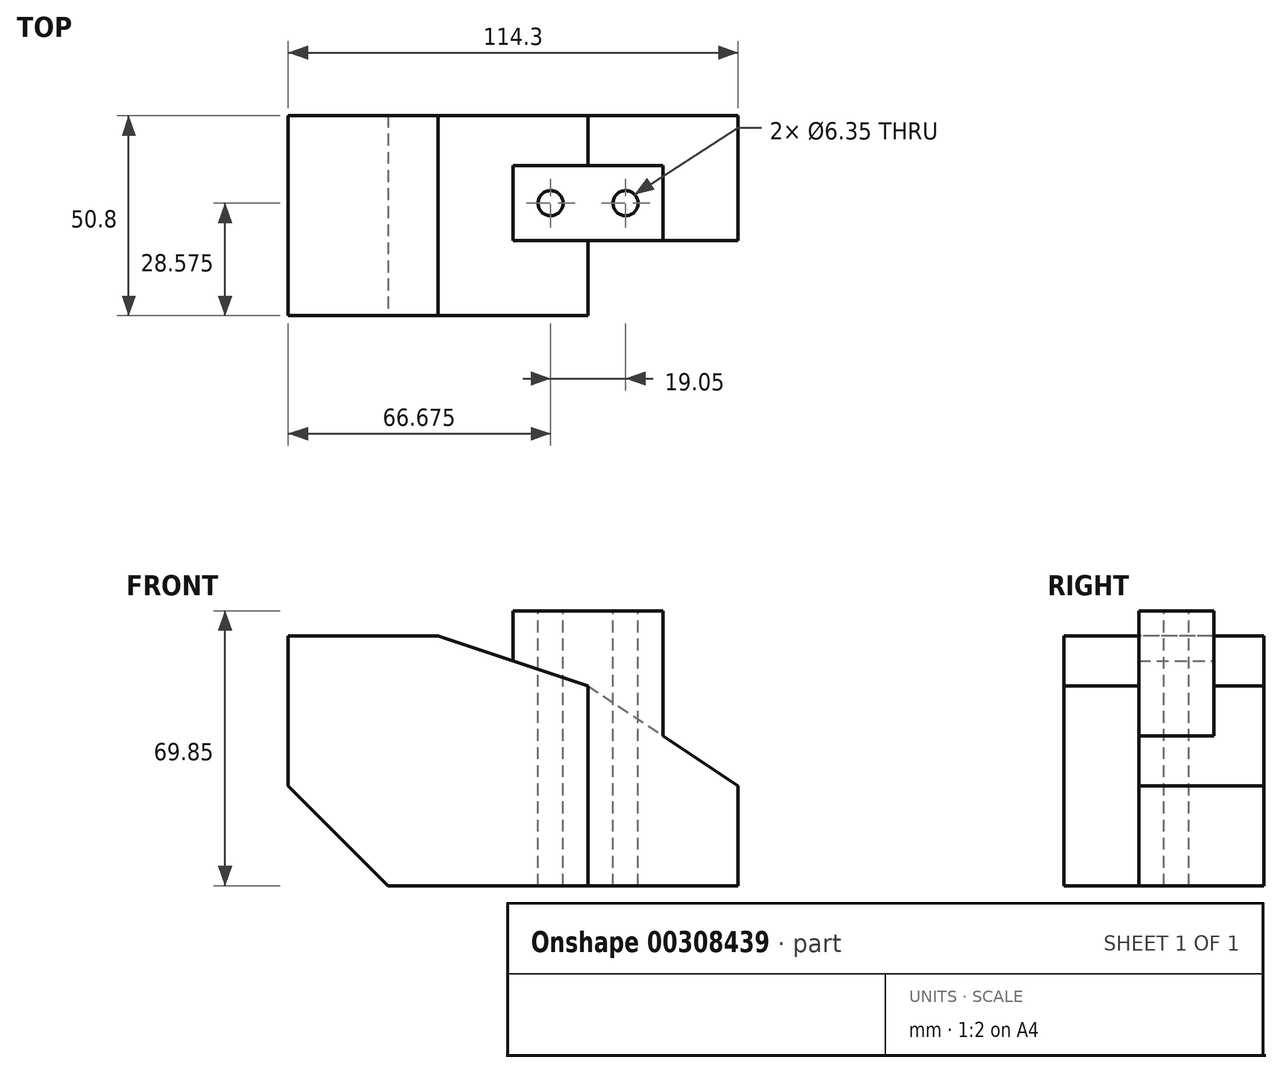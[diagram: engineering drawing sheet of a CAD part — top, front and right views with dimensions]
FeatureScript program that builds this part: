
annotation { "Feature Type Name" : "Feature", "Feature Type Description" : "" }
export const myFeature = defineFeature(function(context is Context, id is Id, definition is map)
    precondition{}
    {
        {
            var Q0;
            Q0=qCreatedBy(makeId("Front.planeOp"),FACE);
            var sketch = newSketch(context, id + "F0", { "sketchPlane" : qUnion([Q0])});
            skLineSegment(sketch, "E0", {"start": v(0, 0) * mm, "end": v(0, 38.1) * mm});
            skLineSegment(sketch, "E1", {"start": v(0, 0) * mm, "end": v(25.4, -25.4) * mm});
            skLineSegment(sketch, "E2", {"start": v(25.4, -25.4) * mm, "end": v(76.2, -25.4) * mm});
            skLineSegment(sketch, "E3", {"start": v(76.2, -25.4) * mm, "end": v(114.3, -25.4) * mm});
            skLineSegment(sketch, "E4", {"start": v(114.3, -25.4) * mm, "end": v(114.3, 38.1) * mm});
            skLineSegment(sketch, "E5", {"start": v(0, 38.1) * mm, "end": v(114.3, 38.1) * mm});
            skSolve(sketch);
        }
        {
            var Q0;
            Q0 = qSketchRegion(id + "F0", true);
            extrude(context, id + "F1", {"entities" : qUnion([Q0]), "oppositeDirection" : true, "depth" : 50.8 * mm});
        }
        {
            var Q0;
            Q0=qCreatedBy(makeId("Top.planeOp"),FACE);
            var sketch = newSketch(context, id + "F2", { "sketchPlane" : qUnion([Q0])});
            skLineSegment(sketch, "E6", {"start": v(114.3, 0) * mm, "end": v(114.3, 19.05) * mm});
            skLineSegment(sketch, "E7", {"start": v(114.3, 0) * mm, "end": v(76.2, 0) * mm});
            skLineSegment(sketch, "E8", {"start": v(76.2, 0) * mm, "end": v(76.2, 19.05) * mm});
            skLineSegment(sketch, "E9", {"start": v(76.2, 19.05) * mm, "end": v(114.3, 19.05) * mm});
            skSolve(sketch);
        }
        {
            var Q0;
            Q0 = qSketchRegion(id + "F2", true);
            extrude(context, id + "F3", {"entities" : qUnion([Q0]), "operationType" : NewBodyOperationType.REMOVE, "endBound" : BoundingType.SYMMETRIC, "oppositeDirection" : true, "depth" : 254 * mm});
        }
        {
            var Q0;
            Q0=qCreatedBy(makeId("Front.planeOp"),FACE);
            var sketch = newSketch(context, id + "F4", { "sketchPlane" : qUnion([Q0])});
            skLineSegment(sketch, "E10", {"start": v(76.2, 38.1) * mm, "end": v(38.1, 38.1) * mm});
            skLineSegment(sketch, "E11", {"start": v(76.2, 38.1) * mm, "end": v(76.2, 25.4) * mm});
            skLineSegment(sketch, "E12", {"start": v(38.1, 38.1) * mm, "end": v(76.2, 25.4) * mm});
            skSolve(sketch);
        }
        {
            var Q0;
            Q0 = qSketchRegion(id + "F4", true);
            extrude(context, id + "F5", {"entities" : qUnion([Q0]), "operationType" : NewBodyOperationType.REMOVE, "endBound" : BoundingType.THROUGH_ALL, "oppositeDirection" : true, "depth" : 25.4 * mm});
        }
        {
            var Q0;
            Q0=makeQuery(id+"F3.boolean.opBoolean","COPY",FACE,{"derivedFrom":makeQuery(id+"F3.opExtrude","SWEPT_FACE",FACE,{"disambiguationData":[OSD([sQuery(id+"F2.wireOp",EDGE,"E9")])]})});
            var sketch = newSketch(context, id + "F6", { "sketchPlane" : qUnion([Q0])});
            skLineSegment(sketch, "E13", {"start": v(114.3, -25.4) * mm, "end": v(114.3, 0) * mm});
            skLineSegment(sketch, "E14", {"start": v(114.3, 0) * mm, "end": v(114.3, 38.1) * mm});
            skLineSegment(sketch, "E15", {"start": v(76.2, 38.1) * mm, "end": v(114.3, 38.1) * mm});
            skLineSegment(sketch, "E16", {"start": v(76.2, 25.4) * mm, "end": v(114.3, 0) * mm});
            skLineSegment(sketch, "E17", {"start": v(76.2, 25.4) * mm, "end": v(76.2, 38.1) * mm});
            skSolve(sketch);
        }
        {
            var Q0;
            Q0 = qSketchRegion(id + "F6", true);
            extrude(context, id + "F7", {"entities" : qUnion([Q0]), "operationType" : NewBodyOperationType.REMOVE, "endBound" : BoundingType.THROUGH_ALL, "oppositeDirection" : true, "depth" : 25.4 * mm});
        }
        {
            var Q0;
            Q0=qCreatedBy(makeId("Top.planeOp"),FACE);
            var sketch = newSketch(context, id + "F8", { "sketchPlane" : qUnion([Q0])});
            skLineSegment(sketch, "E18", {"start": v(76.2, 0) * mm, "end": v(76.2, 19.05) * mm});
            skLineSegment(sketch, "E19", {"start": v(76.2, 19.05) * mm, "end": v(57.15, 19.05) * mm});
            skLineSegment(sketch, "E20", {"start": v(57.15, 19.05) * mm, "end": v(57.15, 38.1) * mm});
            skLineSegment(sketch, "E21", {"start": v(57.15, 38.1) * mm, "end": v(95.25, 38.1) * mm});
            skLineSegment(sketch, "E22", {"start": v(95.25, 38.1) * mm, "end": v(95.25, 19.05) * mm});
            skLineSegment(sketch, "E23", {"start": v(76.2, 19.05) * mm, "end": v(95.25, 19.05) * mm});
            skSolve(sketch);
        }
        {
            var Q0;
            Q0 = qSketchRegion(id + "F8", true);
            extrude(context, id + "F9", {"entities" : qUnion([Q0]), "operationType" : NewBodyOperationType.ADD, "depth" : 44.45 * mm});
        }
        {
            var Q0;
            Q0=makeQuery(id+"F9.opExtrude","CAP_FACE",FACE,{"disambiguationData":[OSD([sQuery(id+"F8.wireOp",EDGE,"E19"),sQuery(id+"F8.wireOp",EDGE,"E20"),sQuery(id+"F8.wireOp",EDGE,"E21"),sQuery(id+"F8.wireOp",EDGE,"E22"),sQuery(id+"F8.wireOp",EDGE,"E23")])],"isStart":false});
            var sketch = newSketch(context, id + "F10", { "sketchPlane" : qUnion([Q0])});
            skCircle(sketch, "E24", {"center": v(66.68, 28.57) * mm, "radius": 3.18 * mm});
            skPoint(sketch, "E24.centerSnap0", {"position": v(57.15, 28.57) * mm});
            skCircle(sketch, "E25", {"center": v(85.73, 28.57) * mm, "radius": 3.18 * mm});
            skPoint(sketch, "E25.centerSnap0", {"position": v(95.25, 28.57) * mm});
            skSolve(sketch);
        }
        {
            var Q0;
            Q0 = qSketchRegion(id + "F10", true);
            extrude(context, id + "F11", {"entities" : qUnion([Q0]), "operationType" : NewBodyOperationType.REMOVE, "endBound" : BoundingType.THROUGH_ALL, "oppositeDirection" : true, "depth" : 25.4 * mm});
        }
    });
